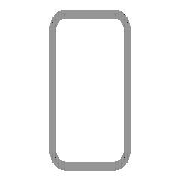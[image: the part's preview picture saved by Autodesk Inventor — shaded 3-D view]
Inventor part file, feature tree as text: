
AUTODESK INVENTOR PART (.ipt)
format: ipt  version: 2025 (Build 290162010, 162A)  size: 133,632 bytes
history: native  units: mm (DEFAULTED — no unit token found)
features: other x4, sketch x1, plane x1
ambient origin geometry x8: Origin, YZ Plane, XZ Plane, XY Plane, X Axis, Y Axis, Z Axis, Center Point
bodies: Solid1 (feature_tree), Body (feature_tree)
feature tree (6):
  parser-record x1  (decoder bookkeeping rows leaked as tree rows — omitted from the tree; the rows remain in map.json)
  other  "Driven Length"
  other  "Start Plane"
  other  "End Plane"
  sketch  "Sketch3"  dims[d3=1020.0mm d4=0.0mm d7=6.0mm d9=40.0mm d11=60.0mm d12=3.0mm d13=40.0mm d14=1060.0mm d15=20.0mm d16=30.0mm d17=90.0deg d18=1020.0mm]
  plane  "Work Plane3"
